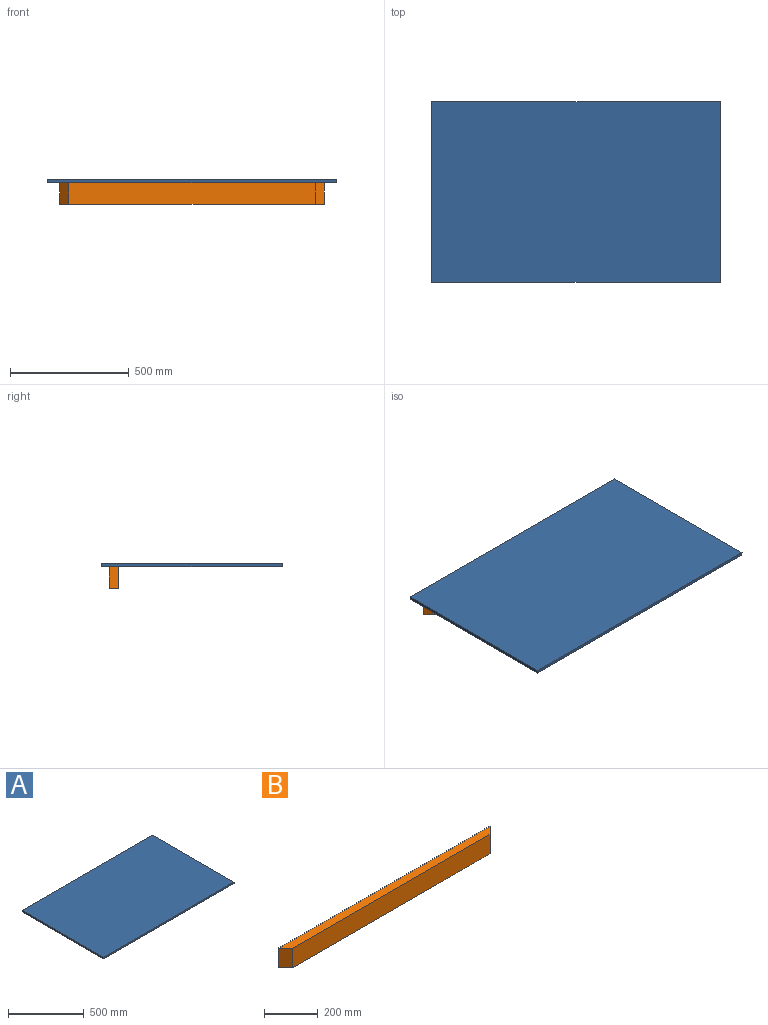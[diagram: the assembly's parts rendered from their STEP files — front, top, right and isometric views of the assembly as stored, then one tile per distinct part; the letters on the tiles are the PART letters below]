
ASSEMBLY  parts=2 mates=1
PART A: 6 faces, bbox 1219.2x762x12.7 mm
  f0: plane 1219.2x12.7mm, normal (0,-1,0), area 15483.8mm2, adj f1,f3,f4,f5
  f1: plane 762x12.7mm, normal (1,0,0), area 9677.4mm2, adj f0,f2,f4,f5
  f2: plane 1219.2x12.7mm, normal (0,1,0), area 15483.8mm2, adj f1,f3,f4,f5
  f3: plane 762x12.7mm, normal (-1,0,0), area 9677.4mm2, adj f0,f2,f4,f5
  f4: plane 1219.2x762mm, normal (0,0,-1), area 929030.4mm2, adj f0,f1,f2,f3
  f5: plane 1219.2x762mm, normal (0,0,1), area 929030.4mm2, adj f0,f1,f2,f3
PART B: 6 faces, bbox 1117.6x38.1x88.9 mm
  f0: plane 88.9x38.1mm, normal (0.71,-0.71,0), area 4790.1mm2, adj f1,f3,f4,f5
  f1: plane 1117.6x88.9mm, normal (0,1,0), area 99354.6mm2, adj f0,f2,f4,f5
  f2: plane 88.9x38.1mm, normal (-0.71,-0.71,0), area 4790.1mm2, adj f1,f3,f4,f5
  f3: plane 1041.4x88.9mm, normal (0,-1,0), area 92580.5mm2, adj f0,f2,f4,f5
  f4: plane 1117.6x38.1mm, normal (0,0,-1), area 41128.9mm2, adj f0,f1,f2,f3
  f5: plane 1117.6x38.1mm, normal (0,0,1), area 41128.9mm2, adj f0,f1,f2,f3
PLACE A t=(161.98,-267.86,343.43)mm
PLACE B rot(axis=(-0.05,0.89,0.46),0deg) t=(111.18,424.07,330.73)mm
MATE fastened A.f4 <-> B.f5  axis (0,0,-1) through (-447.62,113.14,330.73)mm
